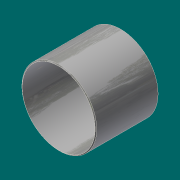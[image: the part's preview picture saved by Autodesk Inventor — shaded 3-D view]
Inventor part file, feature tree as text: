
AUTODESK INVENTOR PART (.ipt)
format: ipt  version: 2017.3 (Build 213256000, 256)  size: 101,376 bytes
history: native  units: in
note: dims shown in document units (in); Inventor stores cm internally (conversion verified against a paired STEP export)
features: chamfer x2, extrude x1, sketch x1
ambient origin geometry x8: Origin, YZ Plane, XZ Plane, XY Plane, X Axis, Y Axis, Z Axis, Center Point
bodies: Solid1 (feature_tree)
feature tree (4):
  extrude  "Extrusion1"  Depth=30.1811in
  chamfer  "Chamfer1"  Distance=30.1811in
  chamfer  "Chamfer2"  Distance=0.4375in
  sketch  "Sketch1"  dims[d0=36.0in d1=35.0in d2=30.1811in d3=0.0in d4=0.4375in d5=0.125in d6=0.2577in d7=0.4375in d8=0.125in d9=0.2577in]
